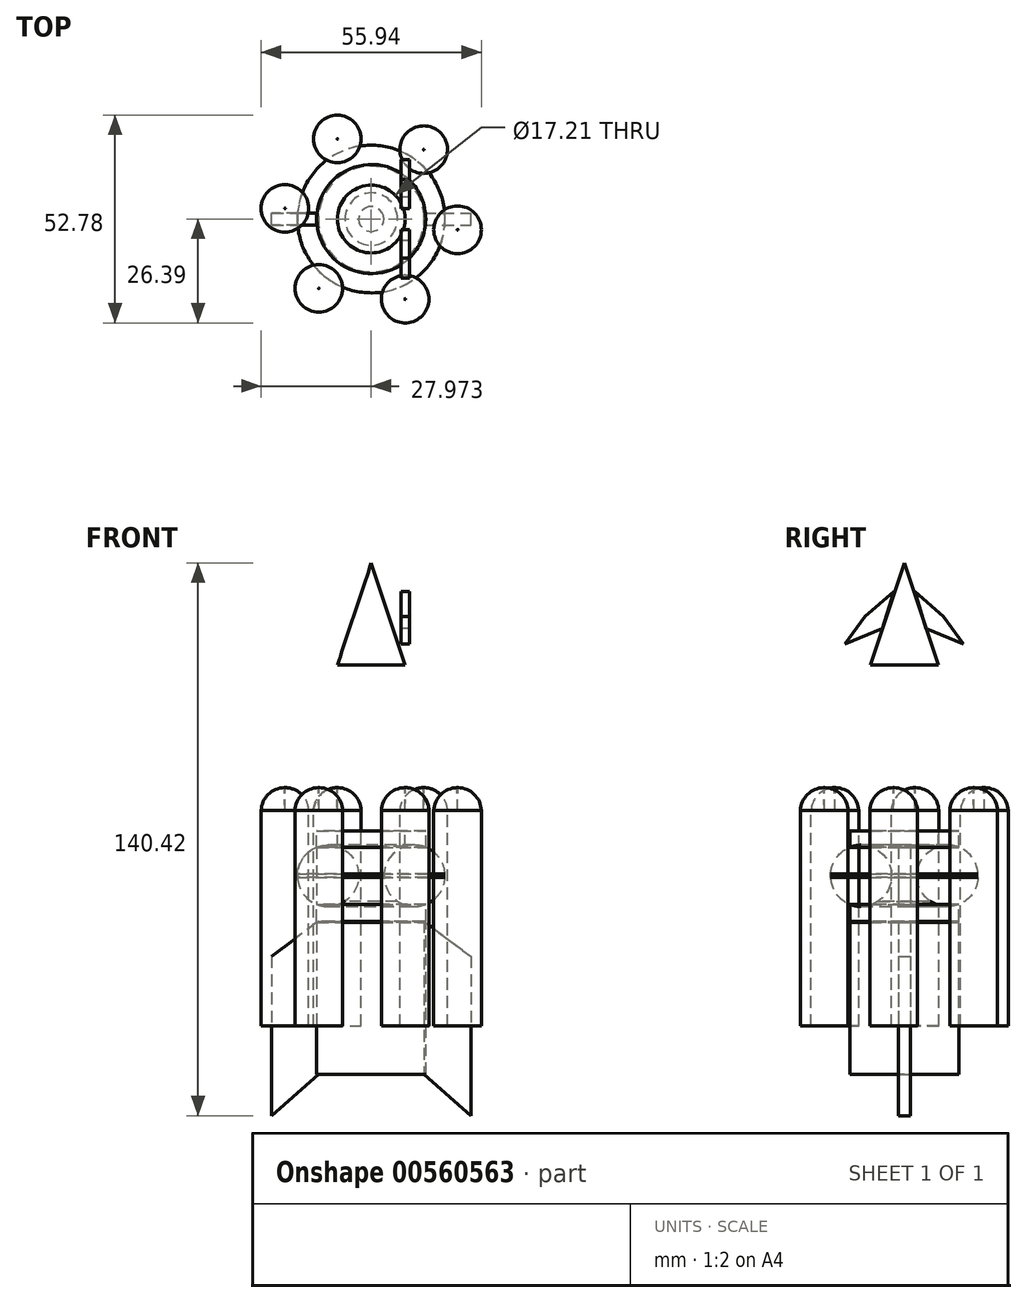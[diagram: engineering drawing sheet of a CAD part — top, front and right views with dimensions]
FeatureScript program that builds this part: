
annotation { "Feature Type Name" : "Feature", "Feature Type Description" : "" }
export const myFeature = defineFeature(function(context is Context, id is Id, definition is map)
    precondition{}
    {
        {
            var Q0;
            Q0=qCreatedBy(makeId("Front.planeOp"),FACE);
            var sketch = newSketch(context, id + "F0", { "sketchPlane" : qUnion([Q0])});
            skLineSegment(sketch, "E0.bottom", {"start": v(-17.21, 35.27) * mm, "end": v(0, 35.27) * mm});
            skLineSegment(sketch, "E0.top", {"start": v(-17.21, -24.73) * mm, "end": v(0, -24.73) * mm});
            skLineSegment(sketch, "E0.left", {"start": v(-17.21, 35.27) * mm, "end": v(-17.21, -24.73) * mm});
            skLineSegment(sketch, "E0.right", {"start": v(0, 35.27) * mm, "end": v(0, -24.73) * mm});
            skLineSegment(sketch, "E1.bottom", {"start": v(-22.47, -6.88) * mm, "end": v(4.8, -6.88) * mm});
            skLineSegment(sketch, "E1.top", {"start": v(-22.47, -68.66) * mm, "end": v(4.8, -68.66) * mm});
            skLineSegment(sketch, "E1.left", {"start": v(-22.47, -6.88) * mm, "end": v(-22.47, -68.66) * mm});
            skLineSegment(sketch, "E1.right", {"start": v(4.8, -6.88) * mm, "end": v(4.8, -68.66) * mm});
            skCircle(sketch, "E2", {"center": v(-19.6, -18.26) * mm, "radius": 7.79 * mm});
            skLineSegment(sketch, "E3", {"start": v(-8.6, 35.27) * mm, "end": v(-8.6, -68.66) * mm, "construction": true});
            skCircle(sketch, "E4.MirrorC", {"center": v(2.38, -18.26) * mm, "radius": 7.79 * mm});
            skLineSegment(sketch, "E5.MirrorCS", {"start": v(5.25, -6.88) * mm, "end": v(-22.02, -6.88) * mm});
            skLineSegment(sketch, "E6", {"start": v(4.8, -29.82) * mm, "end": v(16.68, -38.72) * mm});
            skLineSegment(sketch, "E7", {"start": v(16.68, -38.72) * mm, "end": v(16.68, -79.2) * mm});
            skLineSegment(sketch, "E8", {"start": v(16.68, -79.2) * mm, "end": v(4.8, -68.66) * mm});
            skLineSegment(sketch, "E9", {"start": v(4.8, -29.82) * mm, "end": v(-22.47, -29.82) * mm});
            skLineSegment(sketch, "E10.MirrorCS", {"start": v(-22.02, -29.82) * mm, "end": v(-33.89, -38.72) * mm});
            skLineSegment(sketch, "E11.MirrorCS", {"start": v(-33.89, -38.72) * mm, "end": v(-33.89, -79.2) * mm});
            skLineSegment(sketch, "E12.MirrorCS", {"start": v(-33.89, -79.2) * mm, "end": v(-22.02, -68.66) * mm});
            skLineSegment(sketch, "E13", {"start": v(10.15, -17.83) * mm, "end": v(10.15, -33.83) * mm});
            skLineSegment(sketch, "E14.MirrorCS", {"start": v(-27.37, -17.83) * mm, "end": v(-27.37, -33.83) * mm});
            skLineSegment(sketch, "E15", {"start": v(0, 35.27) * mm, "end": v(-8.6, 61.22) * mm});
            skLineSegment(sketch, "E16", {"start": v(-8.6, 61.22) * mm, "end": v(-17.21, 35.27) * mm});
            skLineSegment(sketch, "E17", {"start": v(-8.6, 61.22) * mm, "end": v(-8.6, 35.27) * mm});
            skLineSegment(sketch, "E18", {"start": v(-8.6, 61.22) * mm, "end": v(-8.6, -68.66) * mm});
            skSolve(sketch);
        }
        {
            var Q0;
            {var subQ0=sQuery(id+"F0.wireOp",EDGE,"E14.MirrorCS");var subQ1=sQuery(id+"F0.wireOp",EDGE,"E2");var subQ2=makeQuery(id+"F0.imprint","INTERSECT",VERTEX,{"disambiguationData":[OD(0.0)],"derivedFrom":[subQ1,subQ0]});Q0=makeQuery(id+"F0.imprint","IMPRINT",FACE,{"disambiguationData":[TD([[makeQuery(id+"F0.imprint","IMPRINT",EDGE,{"disambiguationData":[TD([[subQ2,-1.0]])],"derivedFrom":subQ1}),1.0]])]});}
            var Q1;
            {var subQ0=sQuery(id+"F0.wireOp",EDGE,"E13");var subQ1=sQuery(id+"F0.wireOp",EDGE,"E4.MirrorC");var subQ2=makeQuery(id+"F0.imprint","INTERSECT",VERTEX,{"disambiguationData":[OD(0.0)],"derivedFrom":[subQ1,subQ0]});Q1=makeQuery(id+"F0.imprint","IMPRINT",FACE,{"disambiguationData":[TD([[makeQuery(id+"F0.imprint","IMPRINT",EDGE,{"disambiguationData":[TD([[subQ2,-1.0]])],"derivedFrom":subQ1}),-1.0]])]});}
            var Q2;
            {var subQ0=sQuery(id+"F0.wireOp",EDGE,"E11.MirrorCS");Q2=makeQuery(id+"F0.imprint","IMPRINT",FACE,{"disambiguationData":[TD([[makeQuery(id+"F0.imprint","IMPRINT",EDGE,{"derivedFrom":subQ0}),1.0]])]});}
            var Q3;
            {var subQ0=sQuery(id+"F0.wireOp",EDGE,"E7");Q3=makeQuery(id+"F0.imprint","IMPRINT",FACE,{"disambiguationData":[TD([[makeQuery(id+"F0.imprint","IMPRINT",EDGE,{"derivedFrom":subQ0}),-1.0]])]});}
            extrude(context, id + "F1", {"entities" : qUnion([Q0, Q1, Q2, Q3]), "endBound" : BoundingType.SYMMETRIC, "depth" : 3 * mm, "offsetDistance" : 25 * mm});
        }
        {
            var Q0;
            {var subQ3=sQuery(id+"F0.wireOp",EDGE,"E5.MirrorCS");var subQ6=sQuery(id+"F0.wireOp",EDGE,"E0.left");var subQ8=makeQuery(id+"F0.imprint","INTERSECT",VERTEX,{"derivedFrom":[subQ6,subQ3]});Q0=makeQuery(id+"F0.imprint","IMPRINT",FACE,{"disambiguationData":[TD([[makeQuery(id+"F0.imprint","IMPRINT",EDGE,{"disambiguationData":[TD([[subQ8,1.0]])],"derivedFrom":subQ3}),-1.0]])]});}
            var Q1;
            {var subQ5=sQuery(id+"F0.wireOp",EDGE,"E1.bottom");Q1=makeQuery(id+"F0.imprint","IMPRINT",FACE,{"disambiguationData":[TD([[makeQuery(id+"F0.imprint","IMPRINT",EDGE,{"derivedFrom":subQ5}),-1.0]])]});}
            var Q2;
            {var subQ0=sQuery(id+"F0.wireOp",EDGE,"E1.left");var subQ1=sQuery(id+"F0.wireOp",EDGE,"E1.top");var subQ2=makeQuery(id+"F0.imprint","INTERSECT",VERTEX,{"derivedFrom":[subQ1,subQ0]});Q2=makeQuery(id+"F0.imprint","IMPRINT",FACE,{"disambiguationData":[TD([[makeQuery(id+"F0.imprint","IMPRINT",EDGE,{"disambiguationData":[TD([[subQ2,-1.0]])],"derivedFrom":subQ1}),1.0]])]});}
            var Q3;
            {var subQ0=sQuery(id+"F0.wireOp",EDGE,"E2");var subQ1=sQuery(id+"F0.wireOp",EDGE,"E0.top");var subQ2=makeQuery(id+"F0.imprint","INTERSECT",VERTEX,{"derivedFrom":[subQ1,subQ0]});Q3=makeQuery(id+"F0.imprint","IMPRINT",FACE,{"disambiguationData":[TD([[makeQuery(id+"F0.imprint","IMPRINT",EDGE,{"disambiguationData":[TD([[subQ2,-1.0]])],"derivedFrom":subQ1}),-1.0]])]});}
            var Q4;
            {var subQ0=sQuery(id+"F0.wireOp",EDGE,"E16");Q4=makeQuery(id+"F0.imprint","IMPRINT",FACE,{"disambiguationData":[TD([[makeQuery(id+"F0.imprint","IMPRINT",EDGE,{"derivedFrom":subQ0}),1.0]])]});}
            var Q5;
            Q5=sQuery(id+"F0.wireOp",EDGE,"E17");
            revolve(context, id + "F2", {"entities" : qUnion([Q0, Q1, Q2, Q3, Q4]), "axis" : qUnion([Q5]), "revolveType" : RevolveType.FULL});
        }
        {
            var Q0;
            Q0=qCreatedBy(makeId("Right.planeOp"),FACE);
            var sketch = newSketch(context, id + "F3", { "sketchPlane" : qUnion([Q0])});
            skLineSegment(sketch, "E19", {"start": v(-2.69, 53.94) * mm, "end": v(-9.98, 47.67) * mm});
            skLineSegment(sketch, "E20", {"start": v(-9.98, 47.67) * mm, "end": v(-15.04, 40.58) * mm});
            skLineSegment(sketch, "E21", {"start": v(-15.04, 40.58) * mm, "end": v(-5.52, 44.63) * mm});
            skLineSegment(sketch, "E22", {"start": v(-5.52, 44.63) * mm, "end": v(-2.69, 53.94) * mm});
            skLineSegment(sketch, "E23.MirrorCS", {"start": v(2.69, 53.94) * mm, "end": v(9.98, 47.67) * mm});
            skLineSegment(sketch, "E24.MirrorCS", {"start": v(9.98, 47.67) * mm, "end": v(15.04, 40.58) * mm});
            skLineSegment(sketch, "E25.MirrorCS", {"start": v(15.04, 40.58) * mm, "end": v(5.52, 44.63) * mm});
            skLineSegment(sketch, "E26.MirrorCS", {"start": v(5.52, 44.63) * mm, "end": v(2.69, 53.94) * mm});
            skSolve(sketch);
        }
        {
            var Q0;
            Q0=makeQuery(id+"F3.imprint","IMPRINT",FACE,{"disambiguationData":[TD([[makeQuery(id+"F3.imprint","IMPRINT",EDGE,{"derivedFrom":sQuery(id+"F3.wireOp",EDGE,"E19")}),1.0]])]});
            var Q1;
            Q1=makeQuery(id+"F3.imprint","IMPRINT",FACE,{"disambiguationData":[TD([[makeQuery(id+"F3.imprint","IMPRINT",EDGE,{"derivedFrom":sQuery(id+"F3.wireOp",EDGE,"E23.MirrorCS")}),-1.0]])]});
            extrude(context, id + "F4", {"entities" : qUnion([Q0, Q1]), "endBound" : BoundingType.SYMMETRIC, "depth" : 2.2 * mm, "offsetDistance" : 25 * mm});
        }
        {
            var Q0;
            {var subQ0=sQuery(id+"F0.wireOp",EDGE,"E0.right");var subQ1=sQuery(id+"F0.wireOp",EDGE,"E0.top");var subQ2=makeQuery(id+"F0.imprint","INTERSECT",VERTEX,{"derivedFrom":[subQ1,subQ0]});Q0=makeQuery(id+"F0.imprint","IMPRINT",FACE,{"disambiguationData":[TD([[makeQuery(id+"F0.imprint","IMPRINT",EDGE,{"disambiguationData":[TD([[subQ2,1.0]])],"derivedFrom":subQ1}),1.0]])]});}
            var Q1;
            {var subQ1=sQuery(id+"F0.wireOp",EDGE,"E0.top");var subQ6=sQuery(id+"F0.wireOp",EDGE,"E0.right");var subQ8=makeQuery(id+"F0.imprint","INTERSECT",VERTEX,{"derivedFrom":[subQ1,subQ6]});Q1=makeQuery(id+"F0.imprint","IMPRINT",FACE,{"disambiguationData":[TD([[makeQuery(id+"F0.imprint","IMPRINT",EDGE,{"disambiguationData":[TD([[subQ8,1.0]])],"derivedFrom":subQ1}),-1.0]])]});}
            var Q2;
            {var subQ0=sQuery(id+"F0.wireOp",EDGE,"E4.MirrorC");var subQ1=sQuery(id+"F0.wireOp",EDGE,"E1.right");var subQ2=makeQuery(id+"F0.imprint","INTERSECT",VERTEX,{"disambiguationData":[OD(0.0)],"derivedFrom":[subQ1,subQ0]});Q2=makeQuery(id+"F0.imprint","IMPRINT",FACE,{"disambiguationData":[TD([[makeQuery(id+"F0.imprint","IMPRINT",EDGE,{"disambiguationData":[TD([[subQ2,-1.0]])],"derivedFrom":subQ1}),1.0]])]});}
            var Q3;
            Q3=sQuery(id+"F0.wireOp",EDGE,"E18");
            revolve(context, id + "F5", {"entities" : qUnion([Q0, Q1, Q2]), "axis" : qUnion([Q3]), "revolveType" : RevolveType.FULL});
        }
        {
            var Q0;
            Q0=qCreatedBy(makeId("Right.planeOp"),FACE);
            var sketch = newSketch(context, id + "F6", { "sketchPlane" : qUnion([Q0])});
            skCircle(sketch, "E27", {"center": v(-20.35, -1.9) * mm, "radius": 6.05 * mm});
            skLineSegment(sketch, "E28", {"start": v(-26.4, -1.68) * mm, "end": v(-26.4, -56.41) * mm});
            skLineSegment(sketch, "E29", {"start": v(-26.4, -1.68) * mm, "end": v(-14.3, -1.9) * mm});
            skLineSegment(sketch, "E30", {"start": v(-14.3, -1.9) * mm, "end": v(-14.3, -56.41) * mm});
            skLineSegment(sketch, "E31", {"start": v(-14.3, -56.41) * mm, "end": v(-26.4, -56.41) * mm});
            skLineSegment(sketch, "E32", {"start": v(-20.35, -1.9) * mm, "end": v(-20.35, -56.41) * mm});
            skLineSegment(sketch, "E33.MirrorCS", {"start": v(26.4, -1.68) * mm, "end": v(26.4, -56.41) * mm});
            skLineSegment(sketch, "E34.MirrorCS", {"start": v(20.35, -1.9) * mm, "end": v(20.35, -56.41) * mm});
            skLineSegment(sketch, "E35.MirrorCS", {"start": v(14.3, -1.9) * mm, "end": v(14.3, -56.41) * mm});
            skCircle(sketch, "E36.MirrorC", {"center": v(20.35, -1.9) * mm, "radius": 6.05 * mm});
            skLineSegment(sketch, "E37.MirrorCS", {"start": v(14.3, -56.41) * mm, "end": v(26.4, -56.41) * mm});
            skLineSegment(sketch, "E38.MirrorCS", {"start": v(26.4, -1.68) * mm, "end": v(14.3, -1.9) * mm});
            skLineSegment(sketch, "E39", {"start": v(20.35, -1.9) * mm, "end": v(20.24, 4.15) * mm});
            skLineSegment(sketch, "E40", {"start": v(-20.35, -1.9) * mm, "end": v(-20.45, 4.15) * mm});
            skSolve(sketch);
        }
        {
            var Q0;
            {var subQ0=sQuery(id+"F6.wireOp",EDGE,"E28");var subQ1=sQuery(id+"F6.wireOp",EDGE,"E27");var subQ2=makeQuery(id+"F6.imprint","INTERSECT",VERTEX,{"derivedFrom":[subQ1,subQ0]});Q0=makeQuery(id+"F6.imprint","IMPRINT",FACE,{"disambiguationData":[TD([[makeQuery(id+"F6.imprint","IMPRINT",EDGE,{"disambiguationData":[TD([[subQ2,-1.0]])],"derivedFrom":subQ1}),-1.0]])]});}
            var Q1;
            {var subQ1=sQuery(id+"F6.wireOp",EDGE,"E28");var subQ2=sQuery(id+"F6.wireOp",EDGE,"E27");var subQ4=makeQuery(id+"F6.imprint","INTERSECT",VERTEX,{"derivedFrom":[subQ2,subQ1]});Q1=makeQuery(id+"F6.imprint","IMPRINT",FACE,{"disambiguationData":[TD([[makeQuery(id+"F6.imprint","IMPRINT",EDGE,{"disambiguationData":[TD([[subQ4,-1.0]])],"derivedFrom":subQ2}),1.0]])]});}
            var Q2;
            {var subQ1=sQuery(id+"F6.wireOp",EDGE,"E27");var subQ3=sQuery(id+"F6.wireOp",EDGE,"E40");var subQ4=makeQuery(id+"F6.imprint","INTERSECT",VERTEX,{"derivedFrom":[subQ1,subQ3]});Q2=makeQuery(id+"F6.imprint","IMPRINT",FACE,{"disambiguationData":[TD([[makeQuery(id+"F6.imprint","IMPRINT",EDGE,{"disambiguationData":[TD([[subQ4,1.0]])],"derivedFrom":subQ3}),1.0]])]});}
            var Q3;
            Q3=sQuery(id+"F6.wireOp",EDGE,"E32");
            revolve(context, id + "F7", {"entities" : qUnion([Q0, Q1, Q2]), "axis" : qUnion([Q3]), "revolveType" : RevolveType.FULL});
        }
        {
            var Q0;
            Q0=makeQuery(id+"F7.opRevolve","SWEPT_BODY",BODY,{"disambiguationData":[OSD([sQuery(id+"F6.wireOp",EDGE,"E27"),sQuery(id+"F6.wireOp",EDGE,"E28"),sQuery(id+"F6.wireOp",EDGE,"E31"),sQuery(id+"F6.wireOp",EDGE,"E32"),sQuery(id+"F6.wireOp",EDGE,"E40")])]});
            var Q1;
            Q1=sQuery(id+"F0.wireOp",EDGE,"E18");
            circularPattern(context, id + "F8", {"entities" : qUnion([Q0]), "axis" : qUnion([Q1]), "angle" : 360 * degree, "instanceCount" : 6, "equalSpace" : true});
        }
    });
